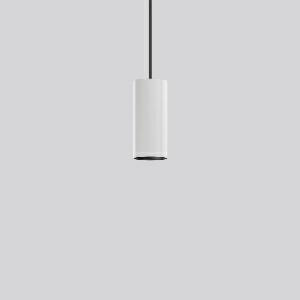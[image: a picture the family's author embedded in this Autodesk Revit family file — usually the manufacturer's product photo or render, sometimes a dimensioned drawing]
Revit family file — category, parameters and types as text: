
# Revit family: deecos_p_mini_911523_002_76_0678
name_source: partatom
category: Lighting Fixtures
units: mm (PartAtom-declared; Revit-internal decimal feet)

## family parameters
Cut with Voids When Loaded = No
Host = Face
Light Source = No
Part Type = Normal
Room Calculation Point = No
Round Connector Dimension = Use Diameter
Shared = No

## types (1)
- DEECOS P mini (1 x LED Modul 930, 3650 lm, 3000)
    Apparent Load = 29 VA
    Approval mark = CE
    CIE Flux Codes = 95 99 100 100 100
    Color Rendering = 90
    Color Temperature = 3000
    Default Elevation = 1800 mm
    Description = Series: DEECOS P mini
Cylindrical pendant luminaire. Housing: die-cast aluminium, powder-coated. Canopy made of powder-coated sheet steel with magnetic attachment. Optical assembly with reflector made of MIRO-Silver with 98% total light reflection for outstanding efficiency - can be changed without tools. Best colour rendering index Ra>90. Transparent pendant cable 5 m, can be shortened, with integrated steel cable. High quality converter without flickering and stroboscopic effect. The following accessories can be mounted without use of tools: interchangeable lenses, honeycomb louvre, clear and frosted diffusers, white interchangeable plastic ring. Decorative recessed suspension set available as accessory.Suitable for accessory Deecos P Tube cylinder extensions 0.5 m, 0.75 m or 1 m. 
Colour: traffic white, matt (RAL 9016)
Diameter: 87 mm
Height: 195 mm
Suspension length: 5000 mm
Lamp: LED
Socket: without socket
Colour temperature: 3000K
Colour rendering index (CRI): 92
System power: 29 W
Rated luminous flux: 3650 lm
Luminous efficiency: 126 lm/W
Control gear: Converter, dimmable, DALI
Protection class: I
Type of protection: IP 20
    Height = 195 mm
    Lamp = 1 x LED Modul 930
    Lamp Light Flux = 3650 lm
    Lamp count = 1
    Length = 87 mm
    Lifetime = 50000 h
    Luminous efficacy = 126 lm/W
    Manufacturer = RZB
    ModVariant = No
    Model = 911523.002.76
    Mounting Place = Ceiling
    Mounting Type = Pendant
    Number of Poles = 1
    OnlyDefault = Yes
    Power Factor = 1
    Product Name = DEECOS P mini
    Product group = Pendant luminaires
    ProductGroupID = 902
    Protection Class = Protection class I
    Protection Degree = IP 20
    RLX_Detail_Level = 1
    RLX_Emergency_Light_Flux = 0 lm
    RLX_Emergency_Type = 0
    RLX_Emergency_Type_DB = No
    RlxData = <blob elided: 54853 chars, md5=b1580425>
    Socket = socket
    Standby Power = 0 W
    System Light Flux = 3650 lm
    System Power = 29 W
    Type Comments = Product without accessories
    Type Image = 911476.002.jpg
    URL = http://relux.com
    VarID = ---
    Voltage = 230 V
    Voltage Range = 220-240 V
    Weight = 0.00 kg
    Width = 0 mm  [stored 0 ft]

note: [stored X ft] marks values corroborated as IEEE doubles in the binary element streams (Revit-internal decimal feet)

## geometry (parser evidence)
native form markers: Blend x4, Sweep x13
no freeform markers — native parametric forms only
